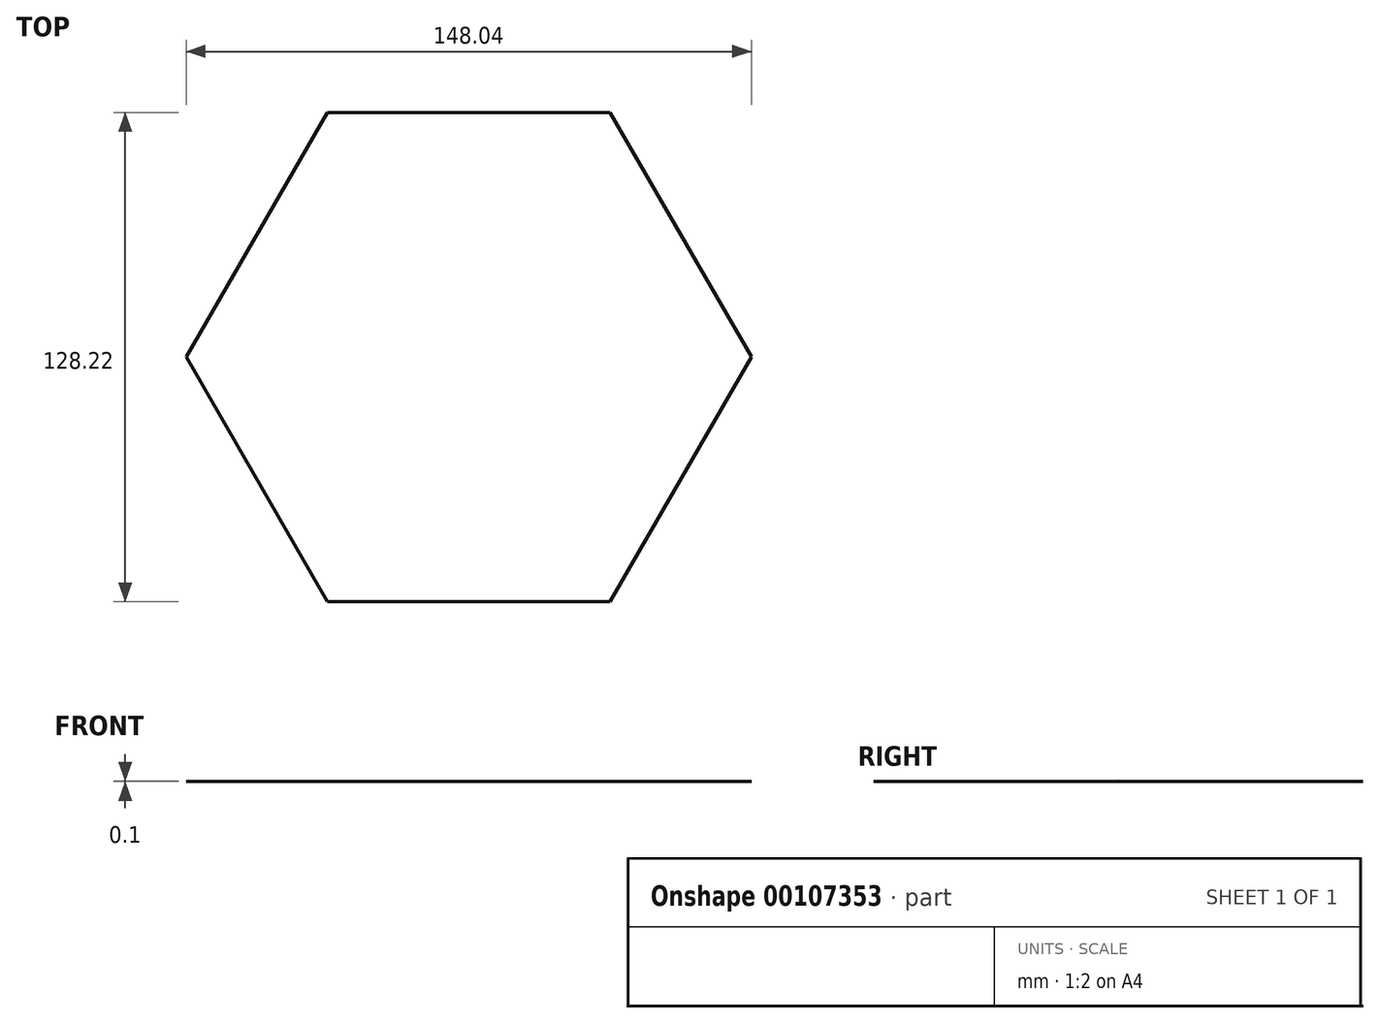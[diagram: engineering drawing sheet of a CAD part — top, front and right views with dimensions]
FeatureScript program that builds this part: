
annotation { "Feature Type Name" : "Feature", "Feature Type Description" : "" }
export const myFeature = defineFeature(function(context is Context, id is Id, definition is map)
    precondition{}
    {
        {
            var Q0;
            Q0=qCreatedBy(makeId("Top.planeOp"),FACE);
            var sketch = newSketch(context, id + "F0", { "sketchPlane" : qUnion([Q0])});
            skCircle(sketch, "E0.cCircle", {"center": v(0, 0) * mm, "radius": 64.1 * mm, "construction": true});
            skLineSegment(sketch, "E0.0", {"start": v(-74.02, 0) * mm, "end": v(-37.01, 64.1) * mm});
            skLineSegment(sketch, "E0.1", {"start": v(-37.01, 64.1) * mm, "end": v(37.01, 64.1) * mm});
            skLineSegment(sketch, "E0.2", {"start": v(37.01, 64.1) * mm, "end": v(74.02, 0) * mm});
            skLineSegment(sketch, "E0.3", {"start": v(74.02, 0) * mm, "end": v(37.01, -64.1) * mm});
            skLineSegment(sketch, "E0.4", {"start": v(37.01, -64.1) * mm, "end": v(-37.01, -64.1) * mm});
            skLineSegment(sketch, "E0.5", {"start": v(-37.01, -64.1) * mm, "end": v(-74.02, 0) * mm});
            skPoint(sketch, "E0.0.midPoint", {"position": v(-55.52, 32.05) * mm});
            skSolve(sketch);
        }
        {
            var Q0;
            Q0=qCreatedBy(makeId("Top.planeOp"),FACE);
            cPlane(context, id + "F1", {"entities" : qUnion([Q0]), "cplaneType" : CPlaneType.OFFSET, "offset" : .1 * mm, "width" : 150 * mm, "height" : 150 * mm});
        }
        {
            var Q0;
            Q0=qCreatedBy(id+"F1.planeOp",FACE);
            var sketch = newSketch(context, id + "F2", { "sketchPlane" : qUnion([Q0])});
            skPoint(sketch, "E1", {"position": v(0, 0) * mm});
            skSolve(sketch);
        }
        {
            var Q0;
            Q0=sQuery(id+"F2.wireOp",VERTEX,"E1");
            var Q1;
            Q1 = qConstructionFilter(qBodyType(qCreatedBy(id + "F0" ,EDGE), BodyType.WIRE), ConstructionObject.NO);
            loft(context, id + "F3", {"bodyType" : ToolBodyType.SURFACE, "wireProfilesArray" : [{ "wireProfileEntities" : qUnion([Q0]) }, { "wireProfileEntities" : qUnion([Q1]) }]});
        }
    });
